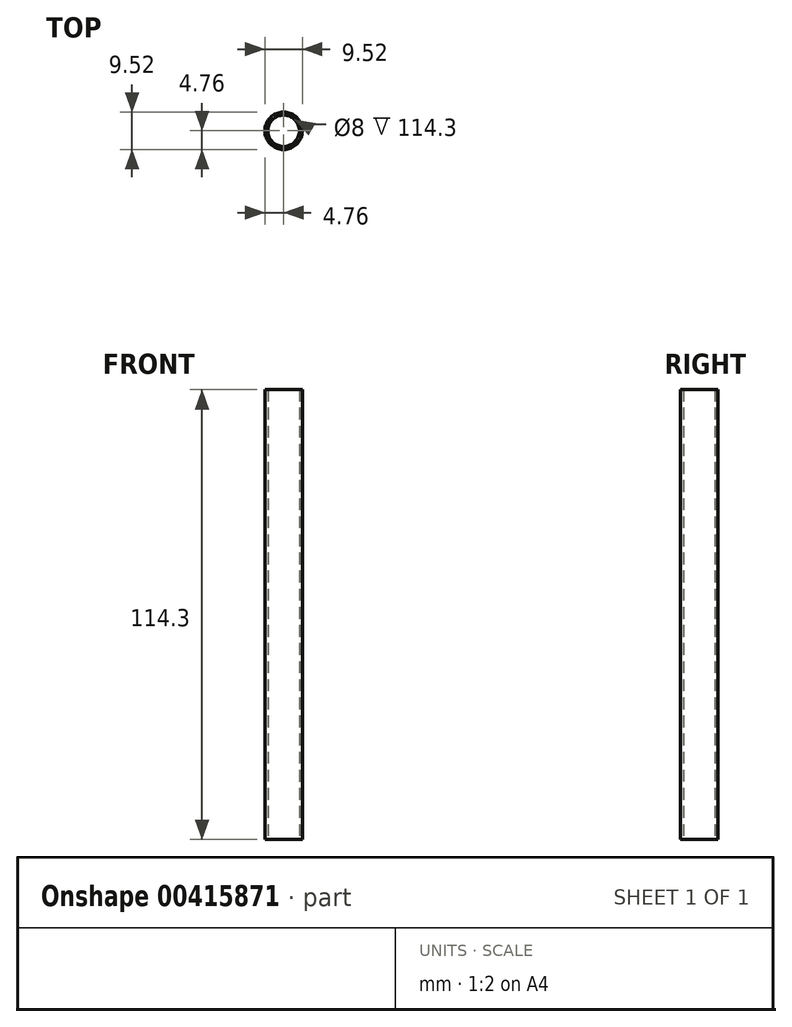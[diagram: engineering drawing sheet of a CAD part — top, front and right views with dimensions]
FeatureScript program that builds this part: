
annotation { "Feature Type Name" : "Feature", "Feature Type Description" : "" }
export const myFeature = defineFeature(function(context is Context, id is Id, definition is map)
    precondition{}
    {
        {
            var Q0;
            Q0=qCreatedBy(makeId("Top.planeOp"),FACE);
            var sketch = newSketch(context, id + "F0", { "sketchPlane" : qUnion([Q0])});
            skCircle(sketch, "E0", {"center": v(0, 0) * mm, "radius": 4.76 * mm});
            skCircle(sketch, "E1.0", {"center": v(0, 0) * mm, "radius": 4 * mm});
            skSolve(sketch);
        }
        {
            var Q0;
            Q0=qSketchRegion(id+"F0",true);
            extrude(context, id + "F1", {"entities" : qUnion([Q0]), "depth" : 114.3 * mm});
        }
    });
